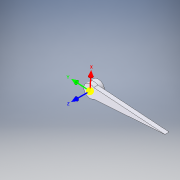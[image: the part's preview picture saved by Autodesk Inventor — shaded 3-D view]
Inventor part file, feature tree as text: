
AUTODESK INVENTOR PART (.ipt)
format: ipt  version: 2019 (Build 230136000, 136)  size: 147,968 bytes
history: native  units: mm
features: other x2, extrude x2, sketch x2
ambient origin geometry x8: Origin, YZ Plane, XZ Plane, XY Plane, X Axis, Y Axis, Z Axis, Center Point
bodies: Solid1 (feature_tree)
feature tree (6):
  other  "Rotational:1"
  other  "<userpath>\OneDrive - Van Ierland\Documents\Inventor\FlightSim\Instrument.xlsx"
  extrude  "Extrusion1"  Depth=1.0mm
  extrude  "Extrusion2"  Depth=1.0mm TaperAngle=0.0deg
  sketch  "Sketch1"  dims[d0=1.0mm d1=3.0mm]
  sketch  "Sketch2"  dims[d3=2.4mm d4=1.0mm d5=0.0mm d6=1.0mm d7=3.0mm d8=20.0mm d9=2.500045mm d10=1.0mm d11=0.0mm d12=0.0mm d13=18.0mm]
